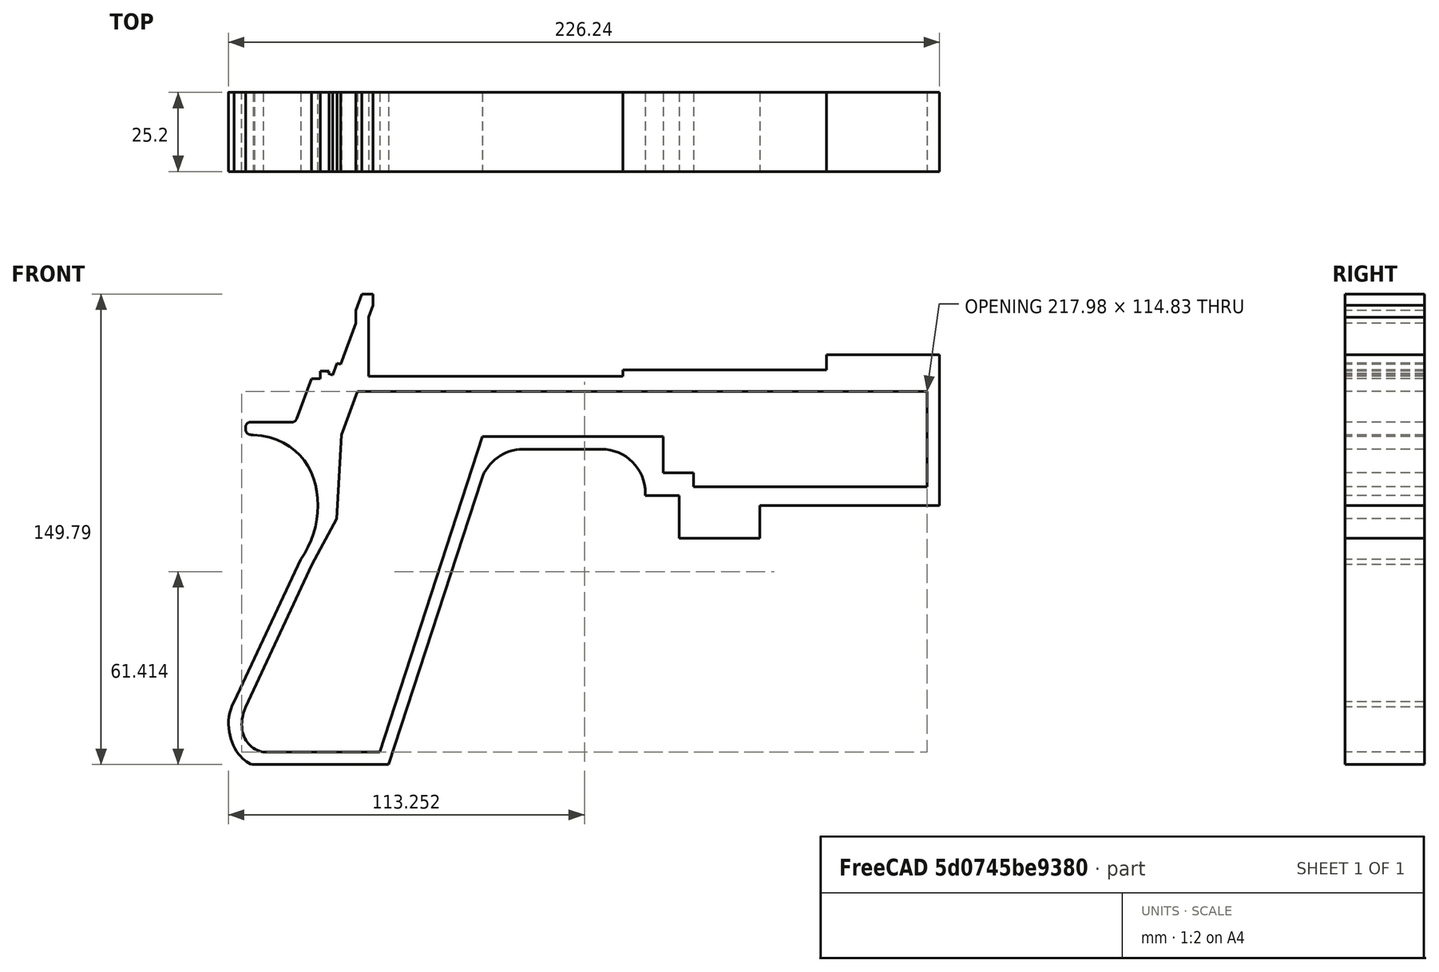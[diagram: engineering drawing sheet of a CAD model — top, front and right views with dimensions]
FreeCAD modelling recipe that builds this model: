
FCSTD DOCUMENT  (FreeCAD 1.0R39319 (Git))
Label: PICON-OF-interno-esterno-estrusione
License: All rights reserved
LicenseURL: https://en.wikipedia.org/wiki/All_rights_reserved
objects: Sketcher::SketchObject×1, PartDesign::Body×1, Part::Extrusion×1
note: 4 computed .brp shape members not serialized (recipe doc carries the construction recipe); baked Part::Feature solids carry a one-line shape summary decoded from their .brp

FEATURE [Sketcher::SketchObject] Sketch
  ArcFitTolerance = 1e-06
  AttachmentSupport = -> [XZ_Plane]
  FullyConstrained = false
  MakeInternals = false
  MapMode = 5
  Placement = pos=(0,0,0) rot=(1,0,0;1.5708rad)
  sketch-geometry (80):
    g0: LineSegment StartX=0 StartY=0 StartZ=0 EndX=-57.2 EndY=0 EndZ=0
    g1: LineSegment StartX=-57.2 StartY=0 StartZ=0 EndX=-57.2 EndY=-10.4 EndZ=0
    g2: LineSegment StartX=-57.2 StartY=-10.4 StartZ=0 EndX=-82.8 EndY=-10.4 EndZ=0
    g3: LineSegment StartX=-82.8 StartY=-10.4 StartZ=0 EndX=-82.8 EndY=3.2 EndZ=0
    g4: LineSegment StartX=-82.8 StartY=3.2 StartZ=0 EndX=-93.6 EndY=3.2 EndZ=0
    g5: LineSegment StartX=-93.6 StartY=3.2 StartZ=0 EndX=-93.6 EndY=4 EndZ=0
    g6: LineSegment StartX=-107.6 StartY=18 StartZ=0 EndX=-132.428 EndY=18 EndZ=0
    g7: LineSegment StartX=-145.743 StartY=8.32624 StartZ=0 EndX=-175.232 EndY=-82.4316 EndZ=0
    g8: LineSegment StartX=-175.232 StartY=-82.4316 StartZ=0 EndX=-218.032 EndY=-82.4316 EndZ=0
    g9: LineSegment StartX=-224.432 StartY=-62.4316 StartZ=0 EndX=-203.301 EndY=-17.1162 EndZ=0
    g10: LineSegment StartX=-204.528 StartY=27.6697 StartZ=0 EndX=-199.861 EndY=40.4914 EndZ=0
    g11: LineSegment StartX=-199.861 StartY=40.4914 StartZ=0 EndX=-197.061 EndY=40.4914 EndZ=0
    g12: LineSegment StartX=-197.061 StartY=40.4914 StartZ=0 EndX=-197.061 EndY=42.8914 EndZ=0
    g13: LineSegment StartX=-197.061 StartY=42.8914 StartZ=0 EndX=-194.261 EndY=42.8914 EndZ=0
    g14: LineSegment StartX=-194.261 StartY=42.8914 StartZ=0 EndX=-194.535 EndY=42.1397 EndZ=0
    g15: LineSegment StartX=-194.535 StartY=42.1397 StartZ=0 EndX=-193.031 EndY=41.5924 EndZ=0
    g16: LineSegment StartX=-193.031 StartY=41.5924 StartZ=0 EndX=-191.663 EndY=45.3512 EndZ=0
    g17: LineSegment StartX=-191.663 StartY=45.3512 StartZ=0 EndX=-190.536 EndY=44.9408 EndZ=0
    g18: LineSegment StartX=-190.536 StartY=44.9408 StartZ=0 EndX=-185.747 EndY=58.0965 EndZ=0
    g19: LineSegment StartX=-185.747 StartY=58.0965 StartZ=0 EndX=-185.747 EndY=62.0965 EndZ=0
    g20: LineSegment StartX=-185.747 StartY=62.0965 StartZ=0 EndX=-183.832 EndY=67.3588 EndZ=0
    g21: LineSegment StartX=-183.832 StartY=67.3588 StartZ=0 EndX=-180.232 EndY=67.3588 EndZ=0
    g22: LineSegment StartX=-180.232 StartY=67.3588 StartZ=0 EndX=-180.232 EndY=63.7588 EndZ=0
    g23: LineSegment StartX=-180.232 StartY=63.7588 StartZ=0 EndX=-181.6 EndY=60 EndZ=0
    g24: LineSegment StartX=-181.6 StartY=60 StartZ=0 EndX=-181.6 EndY=41.2 EndZ=0
    g25: LineSegment StartX=-181.6 StartY=41.2 StartZ=0 EndX=-100.8 EndY=41.2 EndZ=0
    g26: LineSegment StartX=-100.8 StartY=41.2 StartZ=0 EndX=-100.8 EndY=43.2 EndZ=0
    g27: LineSegment StartX=-100.8 StartY=43.2 StartZ=0 EndX=-36 EndY=43.2 EndZ=0
    g28: LineSegment StartX=-36 StartY=43.2 StartZ=0 EndX=-36 EndY=48 EndZ=0
    g29: LineSegment StartX=-36 StartY=48 StartZ=0 EndX=0 EndY=48 EndZ=0
    g30: LineSegment StartX=0 StartY=48 StartZ=0 EndX=0 EndY=0 EndZ=0
    g31: LineSegment StartX=-220.735 StartY=24.184 StartZ=0 EndX=-220.735 EndY=25.127 EndZ=0
    g32: LineSegment StartX=-219.278 StartY=26.584 StartZ=0 EndX=-206.078 EndY=26.584 EndZ=0
    g33: LineSegment StartX=-218.335 StartY=22.584 StartZ=0 EndX=-219.135 EndY=22.584 EndZ=0
    g34: GeomPoint [constr] X=-218.032 Y=-82.4316 Z=0
    g35: GeomPoint [constr] X=-224.432 Y=-62.4316 Z=0
    g36: BSplineCurve PolesCount=4 KnotsCount=2 Degree=3 IsPeriodic=0
    g37-g40: Circle [constr] x4 (B-spline internal-alignment scaffolding for g36; pole/knot coordinates omitted)
    g41: GeomPoint [constr] X=-203.301 Y=-17.1162 Z=0
    g42: GeomPoint [constr] X=-197.787 Y=0 Z=0
    g43: GeomPoint [constr] X=-218.335 Y=22.584 Z=0
    g44: BSplineCurve PolesCount=4 KnotsCount=2 Degree=3 IsPeriodic=0
    g45-g48: Circle [constr] x4 (B-spline internal-alignment scaffolding for g44; pole/knot coordinates omitted)
    g49: ArcOfCircle CenterX=-219.278 CenterY=25.127 CenterZ=0 NormalX=0 NormalY=0 NormalZ=1 AngleXU=0 Radius=1.45699 StartAngle=1.5708 EndAngle=3.14159
    g50: GeomPoint [constr] X=-220.735 Y=26.584 Z=0
    g51: ArcOfCircle CenterX=-219.135 CenterY=24.184 CenterZ=0 NormalX=0 NormalY=0 NormalZ=1 AngleXU=0 Radius=1.6 StartAngle=3.14159 EndAngle=4.71239
    g52: GeomPoint [constr] X=-220.735 Y=22.584 Z=0
    g53: ArcOfCircle CenterX=-206.078 CenterY=28.234 CenterZ=0 NormalX=0 NormalY=0 NormalZ=1 AngleXU=0 Radius=1.65 StartAngle=4.71239 EndAngle=5.93412
    g54: GeomPoint [constr] X=-204.923 Y=26.584 Z=0
    g55: LineSegment StartX=-4 StartY=6 StartZ=0 EndX=-4 EndY=36.4 EndZ=0
    g56: LineSegment StartX=-4 StartY=36.4 StartZ=0 EndX=-185.2 EndY=36.4 EndZ=0
    g57: LineSegment StartX=-185.2 StartY=36.4 StartZ=0 EndX=-190.262 EndY=22.4925 EndZ=0
    g58: LineSegment StartX=-190.262 StartY=22.4925 StartZ=0 EndX=-191.834 EndY=-4.20615 EndZ=0
    g59: LineSegment StartX=-215.122 StartY=-78.4316 StartZ=0 EndX=-178.142 EndY=-78.4316 EndZ=0
    g60: LineSegment StartX=-178.142 StartY=-78.4316 StartZ=0 EndX=-145.51 EndY=22 EndZ=0
    g61: LineSegment StartX=-145.51 StartY=22 StartZ=0 EndX=-87.91 EndY=22 EndZ=0
    g62: LineSegment StartX=-87.91 StartY=22 StartZ=0 EndX=-87.91 EndY=10.4 EndZ=0
    g63: LineSegment StartX=-87.91 StartY=10.4 StartZ=0 EndX=-78.31 EndY=10.4 EndZ=0
    g64: LineSegment StartX=-78.31 StartY=10.4 StartZ=0 EndX=-78.31 EndY=6 EndZ=0
    g65: LineSegment StartX=-78.31 StartY=6 StartZ=0 EndX=-4 EndY=6 EndZ=0
    g66: LineSegment StartX=-191.834 StartY=-4.20615 StartZ=0 EndX=-199.676 EndY=-18.8067 EndZ=0
    g67: LineSegment StartX=-199.676 StartY=-18.8067 StartZ=0 EndX=-220.807 EndY=-64.122 EndZ=0
    g68: GeomPoint [constr] X=-215.122 Y=-78.4316 Z=0
    g69: GeomPoint [constr] X=-220.807 Y=-64.122 Z=0
    g70: BSplineCurve PolesCount=4 KnotsCount=2 Degree=3 IsPeriodic=0
    g71-g74: Circle [constr] x4 (B-spline internal-alignment scaffolding for g70; pole/knot coordinates omitted)
    g75: ArcOfCircle CenterX=-132.428 CenterY=4 CenterZ=0 NormalX=0 NormalY=0 NormalZ=1 AngleXU=0 Radius=14 StartAngle=1.5708 EndAngle=2.82743
    g76: GeomPoint [constr] X=-142.6 Y=18 Z=0
    g77: ArcOfCircle CenterX=-107.6 CenterY=4 CenterZ=0 NormalX=0 NormalY=0 NormalZ=1 AngleXU=0 Radius=14 StartAngle=0 EndAngle=1.5708
    g78: GeomPoint [constr] X=-93.6 Y=18 Z=0
    g79: LineSegment [constr] StartX=-220.807 StartY=-64.122 StartZ=0 EndX=-224.432 EndY=-62.4316 EndZ=0
  constraints (199):
    c: Coincident(g-1,g0)
    c: PointOnObject(g0,g-1)
    c: Coincident(g0,g1)
    c: Vertical(g1)
    c: Coincident(g1,g2)
    c: Horizontal(g2)
    c: Coincident(g2,g3)
    c: Vertical(g3)
    c: Coincident(g3,g4)
    c: Coincident(g4,g5)
    c: Vertical(g5)
    c: Horizontal(g6)
    c: Coincident(g7,g8)
    c: Horizontal(g8)
    c: Coincident(g10,g11)
    c: Horizontal(g11)
    c: Coincident(g11,g12)
    c: Vertical(g12)
    c: Coincident(g12,g13)
    c: Horizontal(g13)
    c: Coincident(g13,g14)
    c: Coincident(g14,g15)
    c: Coincident(g15,g16)
    c: Coincident(g16,g17)
    c: Coincident(g17,g18)
    c: Coincident(g18,g19)
    c: Vertical(g19)
    c: Coincident(g19,g20)
    c: Coincident(g20,g21)
    c: Horizontal(g21)
    c: Coincident(g21,g22)
    c: Vertical(g22)
    c: Coincident(g22,g23)
    c: Coincident(g23,g24)
    c: Vertical(g24)
    c: Coincident(g24,g25)
    c: Horizontal(g25)
    c: Coincident(g25,g26)
    c: Vertical(g26)
    c: Coincident(g26,g27)
    c: Horizontal(g27)
    c: Coincident(g27,g28)
    c: Vertical(g28)
    c: Coincident(g28,g29)
    c: PointOnObject(g29,g-2)
    c: Horizontal(g29)
    c: Coincident(g29,g30)
    c: Coincident(g30,g0)
    c: DistanceY(g30,g30) = 48
    c: DistanceY(g1,g1) = 10.4
    c: DistanceX(g0,g0) = 57.2
    c: DistanceX(g2,g2) = 25.6
    c: Horizontal(g4)
    c: DistanceY(g3,g3) = 13.6
    c: DistanceX(g4,g4) = 10.8
    c: DistanceY(g5,g78) = 14.8
    c: DistanceX(g76,g78) = 49
    c: Distance(g7,g76) = 105.6
    c: DistanceX(g29,g29) = 36
    c: DistanceX(g27,g27) = 64.8
    c: DistanceY(g26,g26) = 2
    c: DistanceY(g28,g28) = 4.8
    c: DistanceX(g25,g25) = 80.8
    c: DistanceY(g24,g24) = 18.8
    c: DistanceY(g22,g22) = 3.6
    c: Distance(g23) = 4
    c: Angle(g-1,g23) = 1.22173
    c: DistanceX(g21,g21) = 3.6
    c: Distance(g20) = 5.6
    c: Angle(g-1,g20) = 1.22173
    c: DistanceY(g19,g19) = 4
    c: Distance(g18) = 14
    c: Angle(g-1,g18) = 1.22173
    c: Distance(g17) = 1.2
    c: Distance(g16) = 4
    c: Angle(g16) = 1.22173
    c: Perpendicular(g18,g17)
    c: Distance(g15) = 1.6
    c: Perpendicular(g16,g15)
    c: Distance(g14) = 0.8
    c: DistanceX(g13,g13) = 2.8
    c: Perpendicular(g15,g14)
    c: DistanceY(g12,g12) = 2.4
    c: DistanceX(g11,g11) = 2.8
    c: Distance(g10,g54) = 14.8
    c: Distance(g9) = 50
    c: Angle(g9,g-1) = 2.00713
    c: Horizontal(g32)
    c: Vertical(g31)
    c: DistanceY(g52,g50) = 4
    c: InternalAlignment(g34,g36)
    c: InternalAlignment(g35,g36)
    c: InternalAlignment(g37,g36)
    c: Weight(g37) = 1
    c: InternalAlignment(g38,g36)
    c: InternalAlignment(g39,g36)
    c: Equal(g39,g37)
    c: InternalAlignment(g40,g36)
    c: Equal(g40,g37)
    c: Coincident(g34,g8)
    c: Coincident(g35,g9)
    c: Horizontal(g33)
    c: InternalAlignment(g41,g44)
    c: PointOnObject(g42,g44)
    c: InternalAlignment(g43,g44)
    c: InternalAlignment(g45,g44)
    c: Weight(g45) = 1
    c: InternalAlignment(g46,g44)
    c: Equal(g46,g45)
    c: InternalAlignment(g47,g44)
    c: Equal(g47,g45)
    c: InternalAlignment(g48,g44)
    c: Equal(g48,g45)
    c: Coincident(g41,g9)
    c: Coincident(g43,g33)
    c: DistanceY(g-1,g42) = 0
    c: DistanceY(g36,g36) = 20
    c: PointOnObject(g50,g32)
    c: PointOnObject(g50,g31)
    c: Tangent(g32,g49) = 1.5708
    c: Tangent(g31,g49) = 1.5708
    c: PointOnObject(g52,g31)
    c: PointOnObject(g52,g33)
    c: Tangent(g31,g51) = 1.5708
    c: Tangent(g33,g51) = 1.5708
    c: PointOnObject(g54,g32)
    c: PointOnObject(g54,g10)
    c: Tangent(g32,g53) = -1.5708
    c: Tangent(g10,g53) = -1.5708
    c: DistanceX(g36,g36) = 6.4
    c: DistanceX(g32,g32) = 13.2
    c: Angle(g-1,g10) = 1.22173
    c: Radius(g53) = 1.65
    c: Radius(g51) = 1.6
    c: Distance(g33) = 0.8
    c: Vertical(g55)
    c: Coincident(g55,g56)
    c: Horizontal(g56)
    c: Coincident(g56,g57)
    c: Coincident(g57,g58)
    c: Coincident(g58,g66)
    c: Horizontal(g59)
    c: Coincident(g59,g60)
    c: Coincident(g60,g61)
    c: Horizontal(g61)
    c: Coincident(g61,g62)
    c: Vertical(g62)
    c: Coincident(g62,g63)
    c: Horizontal(g63)
    c: Coincident(g63,g64)
    c: Vertical(g64)
    c: Coincident(g64,g65)
    c: Coincident(g65,g55)
    c: Horizontal(g65)
    c: DistanceY(g0,g55) = 6
    c: DistanceX(g55,g0) = 4
    c: DistanceY(g55,g25) = 4.8
    c: DistanceX(g56,g56) = 181.2
    c: DistanceX(g61,g61) = 57.6
    c: DistanceY(g76,g60) = 4
    c: DistanceX(g60,g76) = 2.91
    c: DistanceY(g62,g62) = 11.6
    c: DistanceX(g63,g63) = 9.6
    c: DistanceY(g7,g59) = 4
    c: Coincident(g66,g67)
    c: Distance(g67) = 50
    c: DistanceX(g36,g59) = 2.91
    c: InternalAlignment(g68,g70)
    c: InternalAlignment(g69,g70)
    c: InternalAlignment(g71,g70)
    c: Weight(g71) = 1
    c: InternalAlignment(g72,g70)
    c: Equal(g72,g71)
    c: InternalAlignment(g73,g70)
    c: Equal(g73,g71)
    c: InternalAlignment(g74,g70)
    c: Equal(g74,g71)
    c: Coincident(g68,g59)
    c: Coincident(g69,g67)
    c: Angle(g-1,g57) = 1.22173
    c: PointOnObject(g76,g7)
    c: PointOnObject(g76,g6)
    c: Tangent(g7,g75) = -1.5708
    c: Tangent(g6,g75) = -1.5708
    c: PointOnObject(g78,g5)
    c: PointOnObject(g78,g6)
    c: Tangent(g5,g77) = -1.5708
    c: Tangent(g6,g77) = -1.5708
    c: Radius(g77) = 14
    c: Radius(g75) = 14
    c: DistanceX(g8,g8) = 42.8
    c: Angle(g7,g-1) = 1.88496
    c: Parallel(g60,g7)
    c: Parallel(g67,g9)
    c: Coincident(g79,g70)
    c: Perpendicular(g67,g79)
    c: Distance(g79) = 4
    c: Coincident(g36,g79)
    c: Distance(g57) = 14.8
FEATURE [PartDesign::Body] Body  label="Corpo"
  AllowCompound = false
  Group = -> [Sketch]
  Origin = -> Origin
FEATURE [Part::Extrusion] Extrude
  Base = -> Sketch
  Dir = (0,-1,2e-16)
  DirMode = 2
  FaceMakerClass = Part::FaceMakerBullseye
  FaceMakerMode = 3
  LengthFwd = 25.2
  LengthRev = 12.6
  Solid = true
  Symmetric = true
